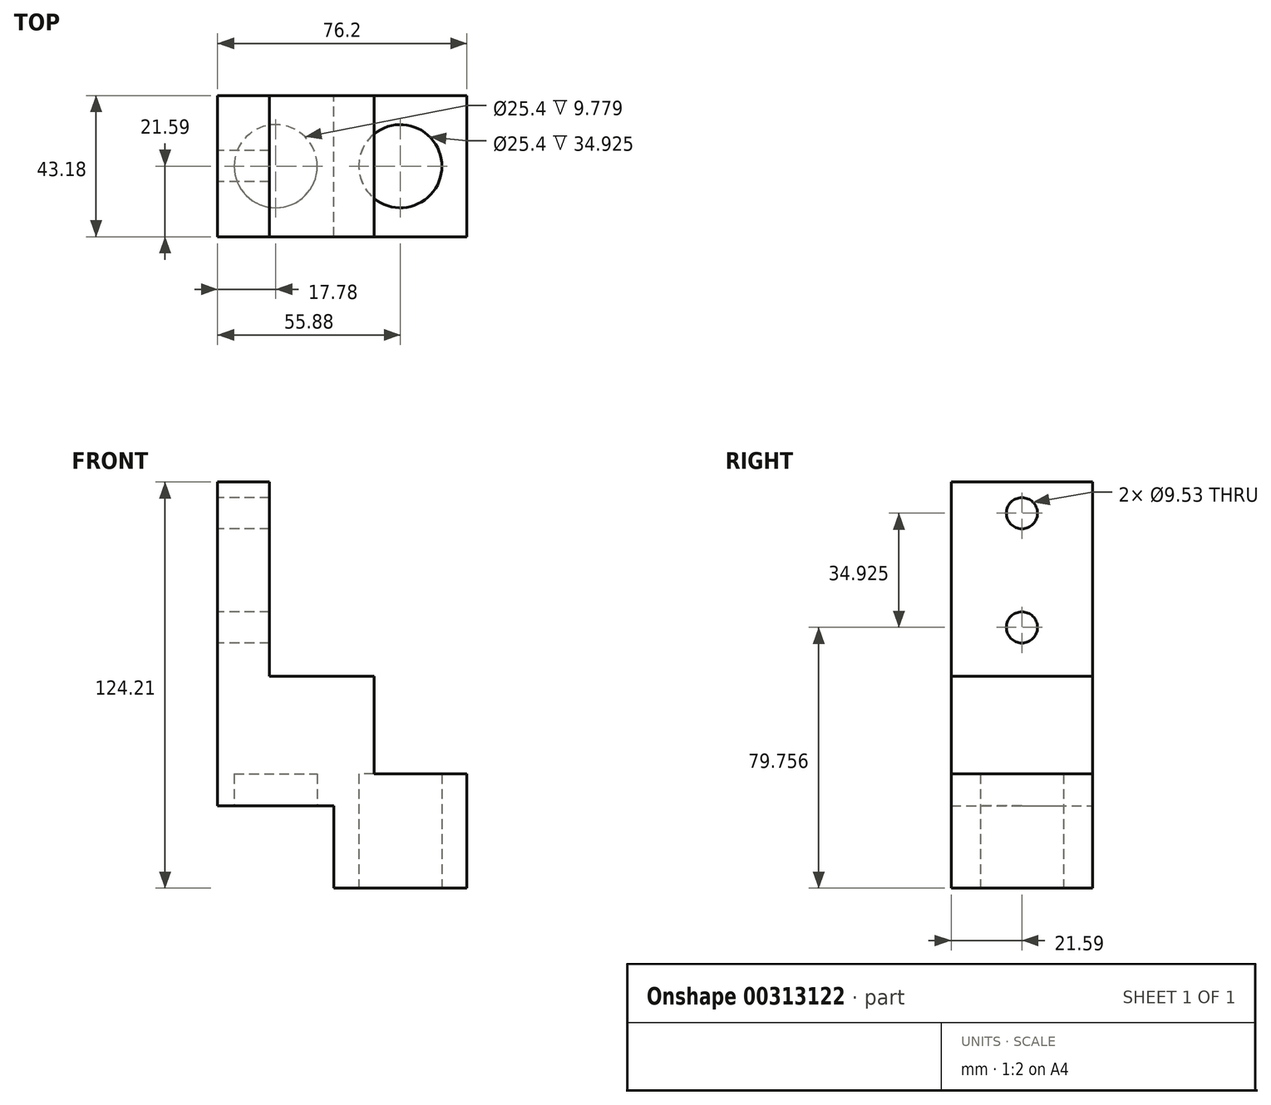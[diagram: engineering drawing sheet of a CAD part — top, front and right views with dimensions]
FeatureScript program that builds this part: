
annotation { "Feature Type Name" : "Feature", "Feature Type Description" : "" }
export const myFeature = defineFeature(function(context is Context, id is Id, definition is map)
    precondition{}
    {
        {
            var Q0;
            Q0=qCreatedBy(makeId("Front.planeOp"),FACE);
            var sketch = newSketch(context, id + "F0", { "sketchPlane" : qUnion([Q0])});
            skLineSegment(sketch, "E0", {"start": v(0, 0) * mm, "end": v(0, 34.93) * mm});
            skLineSegment(sketch, "E1", {"start": v(0, 34.93) * mm, "end": v(-28.4, 34.93) * mm});
            skLineSegment(sketch, "E2", {"start": v(-28.4, 34.93) * mm, "end": v(-28.4, 64.77) * mm});
            skLineSegment(sketch, "E3", {"start": v(-28.4, 64.77) * mm, "end": v(-60.33, 64.77) * mm});
            skLineSegment(sketch, "E4", {"start": v(-60.33, 64.77) * mm, "end": v(-60.33, 124.2) * mm});
            skLineSegment(sketch, "E5", {"start": v(-60.33, 124.2) * mm, "end": v(-76.2, 124.2) * mm});
            skLineSegment(sketch, "E6", {"start": v(-76.2, 124.2) * mm, "end": v(-76.2, 25.15) * mm});
            skLineSegment(sketch, "E7", {"start": v(-76.2, 25.15) * mm, "end": v(-40.64, 25.15) * mm});
            skLineSegment(sketch, "E8", {"start": v(-40.64, 25.15) * mm, "end": v(-40.64, 0) * mm});
            skLineSegment(sketch, "E9", {"start": v(-40.64, 0) * mm, "end": v(0, 0) * mm});
            skSolve(sketch);
        }
        {
            var Q0;
            Q0 = qSketchRegion(id + "F0", true);
            extrude(context, id + "F1", {"entities" : qUnion([Q0]), "endBound" : BoundingType.SYMMETRIC, "depth" : 43.18 * mm});
        }
        {
            var Q0;
            Q0=makeQuery(id+"F1.opExtrude","SWEPT_FACE",FACE,{"disambiguationData":[OSD([sQuery(id+"F0.wireOp",EDGE,"E6")])]});
            var sketch = newSketch(context, id + "F2", { "sketchPlane" : qUnion([Q0])});
            skCircle(sketch, "E10", {"center": v(0, 114.68) * mm, "radius": 4.76 * mm});
            skPoint(sketch, "E10.centerSnap0", {"position": v(0, 124.2) * mm});
            skCircle(sketch, "E11", {"center": v(0, 79.76) * mm, "radius": 4.76 * mm});
            skSolve(sketch);
        }
        {
            var Q0;
            Q0 = qSketchRegion(id + "F2", true);
            extrude(context, id + "F3", {"entities" : qUnion([Q0]), "operationType" : NewBodyOperationType.REMOVE, "endBound" : BoundingType.THROUGH_ALL, "oppositeDirection" : true, "depth" : 25.4 * mm});
        }
        {
            var Q0;
            Q0=makeQuery(id+"F1.opExtrude","SWEPT_FACE",FACE,{"disambiguationData":[OSD([sQuery(id+"F0.wireOp",EDGE,"E7")])]});
            var sketch = newSketch(context, id + "F4", { "sketchPlane" : qUnion([Q0])});
            skCircle(sketch, "E12", {"center": v(-58.42, 0) * mm, "radius": 12.7 * mm});
            skPoint(sketch, "E12.centerSnap0", {"position": v(-76.2, 0) * mm});
            skPoint(sketch, "E12.centerSnap1", {"position": v(-58.42, 21.59) * mm});
            skCircle(sketch, "E13", {"center": v(-20.32, 0) * mm, "radius": 12.7 * mm});
            skSolve(sketch);
        }
        {
            var Q0;
            Q0 = qSketchRegion(id + "F4", true);
            var Q1;
            Q1=makeQuery(id+"F1.opExtrude","SWEPT_FACE",FACE,{"disambiguationData":[OSD([sQuery(id+"F0.wireOp",EDGE,"E1")])]});
            extrude(context, id + "F5", {"entities" : qUnion([Q0]), "operationType" : NewBodyOperationType.REMOVE, "endBound" : BoundingType.UP_TO_SURFACE, "oppositeDirection" : true, "endBoundEntityFace" : qUnion([Q1]), "depth" : 25.4 * mm, "hasSecondDirection" : true, "secondDirectionBound" : SecondDirectionBoundingType.THROUGH_ALL, "secondDirectionOppositeDirection" : false, "secondDirectionDepth" : 25.4 * mm});
        }
    });
